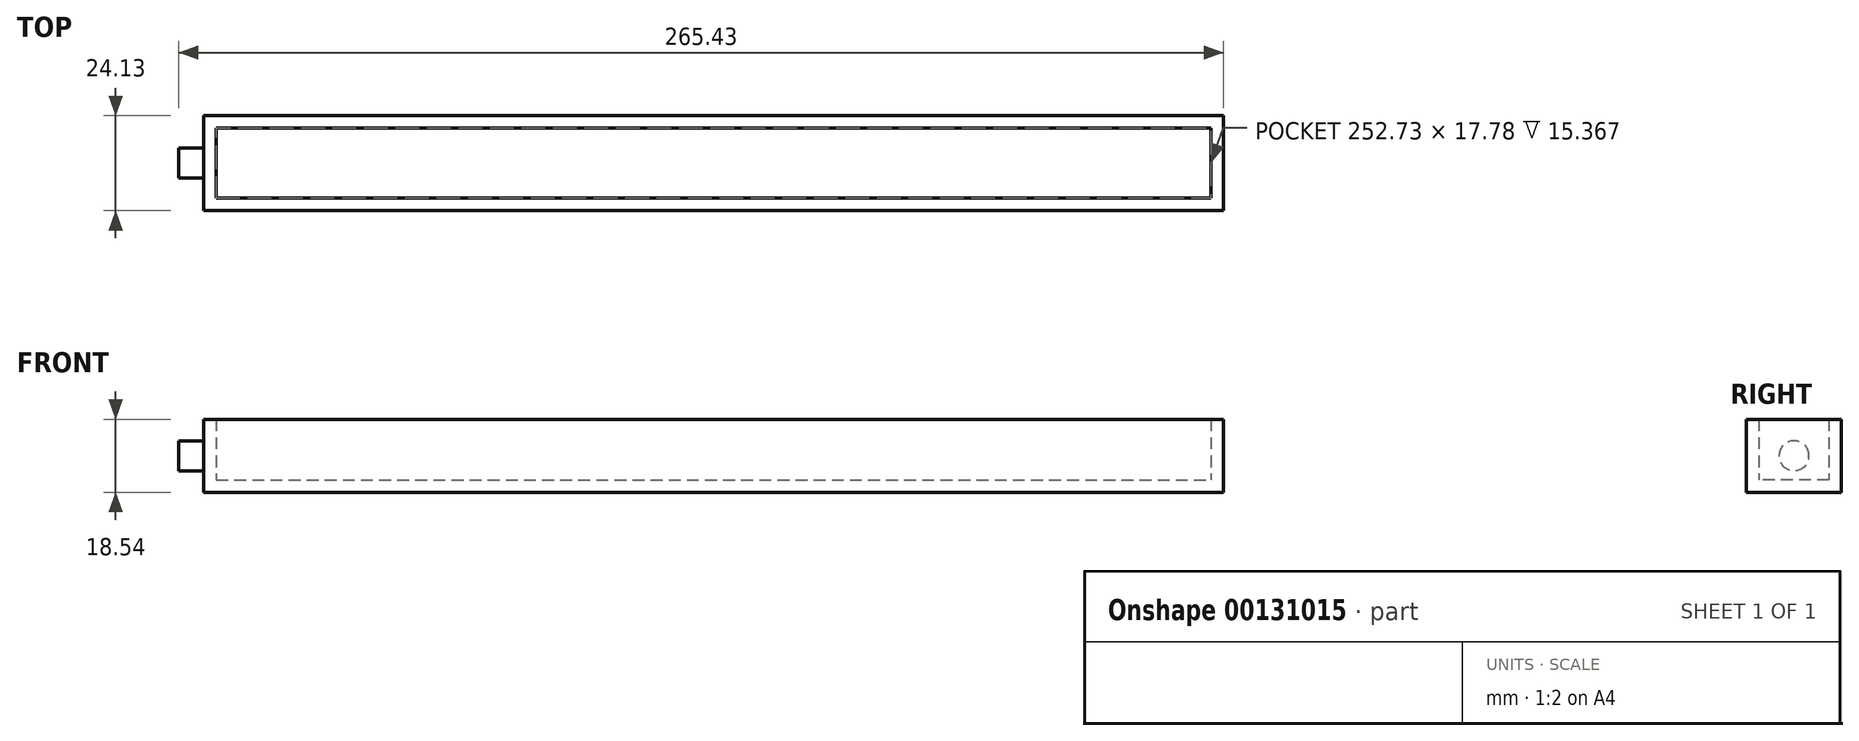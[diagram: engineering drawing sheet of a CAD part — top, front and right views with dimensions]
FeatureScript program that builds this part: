
annotation { "Feature Type Name" : "Feature", "Feature Type Description" : "" }
export const myFeature = defineFeature(function(context is Context, id is Id, definition is map)
    precondition{}
    {
        {
            var Q0;
            Q0=qCreatedBy(makeId("Top.planeOp"),FACE);
            var sketch = newSketch(context, id + "F0", { "sketchPlane" : qUnion([Q0])});
            skLineSegment(sketch, "E0.bottom", {"start": v(-128.08, 2.1) * mm, "end": v(131, 2.1) * mm});
            skLineSegment(sketch, "E0.top", {"start": v(-128.08, -22.03) * mm, "end": v(131, -22.03) * mm});
            skLineSegment(sketch, "E0.left", {"start": v(-128.08, 2.1) * mm, "end": v(-128.08, -22.03) * mm});
            skLineSegment(sketch, "E0.right", {"start": v(131, 2.1) * mm, "end": v(131, -22.03) * mm});
            skLineSegment(sketch, "E1.0", {"start": v(-124.9, -1.08) * mm, "end": v(127.83, -1.08) * mm});
            skLineSegment(sketch, "E1.1", {"start": v(-124.9, -1.08) * mm, "end": v(-124.9, -18.86) * mm});
            skLineSegment(sketch, "E1.2", {"start": v(-124.9, -18.86) * mm, "end": v(127.83, -18.86) * mm});
            skLineSegment(sketch, "E1.3", {"start": v(127.83, -1.08) * mm, "end": v(127.83, -18.86) * mm});
            skSolve(sketch);
        }
        {
            var Q0;
            Q0=makeQuery(id+"F0.imprint","IMPRINT",FACE,{"disambiguationData":[TD([[makeQuery(id+"F0.imprint","IMPRINT",EDGE,{"derivedFrom":sQuery(id+"F0.wireOp",EDGE,"E1.0")}),-1.0]])]});
            extrude(context, id + "F1", {"entities" : qUnion([Q0]), "depth" : 3.17 * mm});
        }
        {
            var Q0;
            Q0=makeQuery(id+"F0.imprint","IMPRINT",FACE,{"disambiguationData":[TD([[makeQuery(id+"F0.imprint","IMPRINT",EDGE,{"derivedFrom":sQuery(id+"F0.wireOp",EDGE,"E0.bottom")}),-1.0]])]});
            extrude(context, id + "F2", {"entities" : qUnion([Q0]), "operationType" : NewBodyOperationType.ADD, "depth" : 18.54 * mm});
        }
        {
            var Q0;
            Q0=makeQuery(id+"F2.opExtrude","SWEPT_FACE",FACE,{"disambiguationData":[OSD([sQuery(id+"F0.wireOp",EDGE,"E0.left")])]});
            var sketch = newSketch(context, id + "F3", { "sketchPlane" : qUnion([Q0])});
            skCircle(sketch, "E2", {"center": v(9.97, 9.27) * mm, "radius": 3.81 * mm});
            skPoint(sketch, "E2.centerSnap0", {"position": v(-2.1, 9.27) * mm});
            skPoint(sketch, "E2.centerSnap1", {"position": v(9.97, 18.54) * mm});
            skSolve(sketch);
        }
        {
            var Q0;
            Q0=makeQuery(id+"F3.imprint","IMPRINT",FACE,{"disambiguationData":[TD([[makeQuery(id+"F3.imprint","IMPRINT",EDGE,{"derivedFrom":sQuery(id+"F3.wireOp",EDGE,"E2")}),1.0]])]});
            extrude(context, id + "F4", {"entities" : qUnion([Q0]), "operationType" : NewBodyOperationType.ADD, "depth" : 6.35 * mm});
        }
    });
